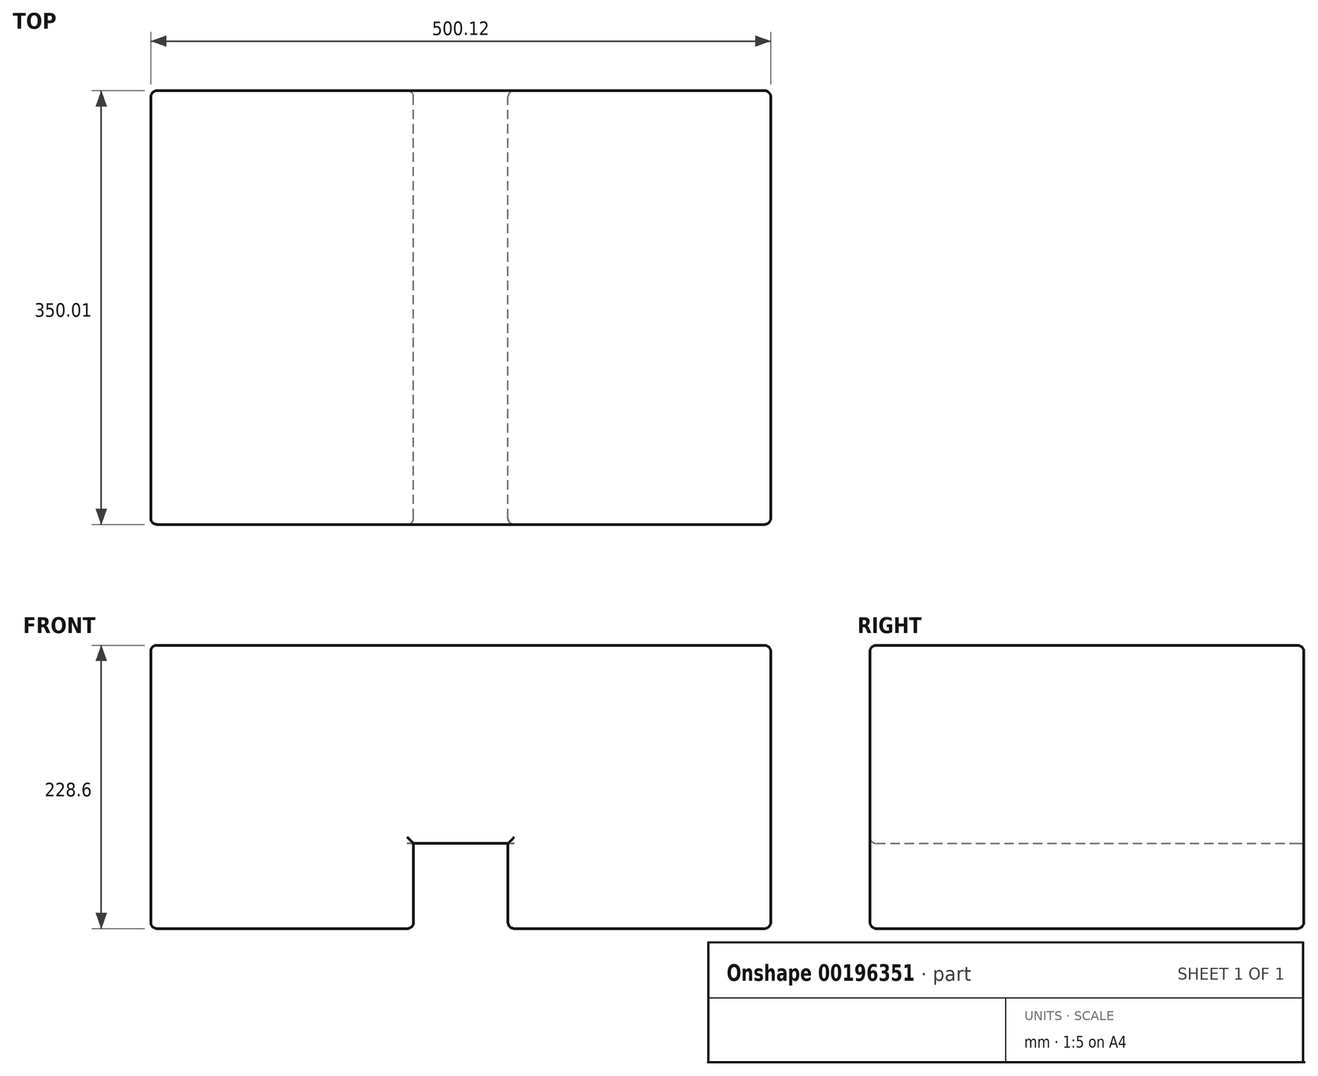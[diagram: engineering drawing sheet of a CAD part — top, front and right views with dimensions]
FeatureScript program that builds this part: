
annotation { "Feature Type Name" : "Feature", "Feature Type Description" : "" }
export const myFeature = defineFeature(function(context is Context, id is Id, definition is map)
    precondition{}
    {
        {
            var Q0;
            Q0=qCreatedBy(makeId("Front.planeOp"),FACE);
            var sketch = newSketch(context, id + "F0", { "sketchPlane" : qUnion([Q0])});
            skLineSegment(sketch, "E0.bottom", {"start": v(250.06, -114.3) * mm, "end": v(-250.06, -114.3) * mm});
            skLineSegment(sketch, "E0.top", {"start": v(250.06, 114.3) * mm, "end": v(-250.06, 114.3) * mm});
            skLineSegment(sketch, "E0.left", {"start": v(250.06, -114.3) * mm, "end": v(250.06, 114.3) * mm});
            skLineSegment(sketch, "E0.right", {"start": v(-250.06, -114.3) * mm, "end": v(-250.06, 114.3) * mm});
            skPoint(sketch, "E0.middle", {"position": v(0, 0) * mm});
            skSolve(sketch);
        }
        {
            var Q0;
            Q0 = qSketchRegion(id + "F0", true);
            extrude(context, id + "F1", {"entities" : qUnion([Q0]), "oppositeDirection" : true, "depth" : 350 * mm});
        }
        {
            var Q0;
            Q0=makeQuery(id+"F1.opExtrude","CAP_FACE",FACE,{"disambiguationData":[OSD([sQuery(id+"F0.wireOp",EDGE,"E0.bottom"),sQuery(id+"F0.wireOp",EDGE,"E0.top"),sQuery(id+"F0.wireOp",EDGE,"E0.left"),sQuery(id+"F0.wireOp",EDGE,"E0.right")])],"isStart":true});
            var Q1;
            Q1=makeQuery(id+"F1.opExtrude","SWEPT_FACE",FACE,{"disambiguationData":[OSD([sQuery(id+"F0.wireOp",EDGE,"E0.right")])]});
            var Q2;
            Q2=makeQuery(id+"F1.opExtrude","SWEPT_FACE",FACE,{"disambiguationData":[OSD([sQuery(id+"F0.wireOp",EDGE,"E0.top")])]});
            var Q3;
            Q3=makeQuery(id+"F1.opExtrude","SWEPT_FACE",FACE,{"disambiguationData":[OSD([sQuery(id+"F0.wireOp",EDGE,"E0.bottom")])]});
            var Q4;
            Q4=makeQuery(id+"F1.opExtrude","SWEPT_FACE",FACE,{"disambiguationData":[OSD([sQuery(id+"F0.wireOp",EDGE,"E0.left")])]});
            fillet(context, id + "F2", {"entities" : qUnion([Q0, Q1, Q2, Q3, Q4]), "radius" : 5.08 * mm, "tangentPropagation" : true, "allowEdgeOverflow" : false});
        }
        {
            var Q0;
            Q0=makeQuery(id+"F1.opExtrude","CAP_FACE",FACE,{"disambiguationData":[OSD([sQuery(id+"F0.wireOp",EDGE,"E0.bottom"),sQuery(id+"F0.wireOp",EDGE,"E0.top"),sQuery(id+"F0.wireOp",EDGE,"E0.left"),sQuery(id+"F0.wireOp",EDGE,"E0.right")])],"isStart":false});
            var sketch = newSketch(context, id + "F3", { "sketchPlane" : qUnion([Q0])});
            skLineSegment(sketch, "E1", {"start": v(0, 0) * mm, "end": v(0, -45.63) * mm});
            skLineSegment(sketch, "E2", {"start": v(0, -121.83) * mm, "end": v(0, -109.22) * mm});
            skLineSegment(sketch, "E3", {"start": v(38.1, -94.1) * mm, "end": v(39.87, -94.1) * mm});
            skLineSegment(sketch, "E4.bottom", {"start": v(38.1, -45.63) * mm, "end": v(-38.1, -45.63) * mm});
            skLineSegment(sketch, "E4.top", {"start": v(38.1, -121.83) * mm, "end": v(-38.1, -121.83) * mm});
            skLineSegment(sketch, "E4.left", {"start": v(38.1, -45.63) * mm, "end": v(38.1, -121.83) * mm});
            skLineSegment(sketch, "E4.right", {"start": v(-38.1, -45.63) * mm, "end": v(-38.1, -121.83) * mm});
            skPoint(sketch, "E4.middle", {"position": v(0, -83.73) * mm});
            skLineSegment(sketch, "E5.trimOffspring", {"start": v(0, -109.22) * mm, "end": v(0, -121.83) * mm});
            skSolve(sketch);
        }
        {
            var Q0;
            Q0 = qSketchRegion(id + "F3", true);
            extrude(context, id + "F4", {"entities" : qUnion([Q0]), "operationType" : NewBodyOperationType.REMOVE, "endBound" : BoundingType.THROUGH_ALL, "oppositeDirection" : true, "depth" : 101.6 * mm});
        }
        {
            var Q0;
            Q0=makeQuery(id+"F4.boolean.opBoolean","INTERSECT",EDGE,{"derivedFrom":[makeQuery(id+"F1.opExtrude","CAP_FACE",FACE,{"disambiguationData":[OSD([sQuery(id+"F0.wireOp",EDGE,"E0.bottom"),sQuery(id+"F0.wireOp",EDGE,"E0.top"),sQuery(id+"F0.wireOp",EDGE,"E0.left"),sQuery(id+"F0.wireOp",EDGE,"E0.right")])],"isStart":true}),makeQuery(id+"F4.opExtrude","SWEPT_FACE",FACE,{"disambiguationData":[OSD([sQuery(id+"F3.wireOp",EDGE,"E4.bottom")])]})]});
            var Q1;
            Q1=makeQuery(id+"F4.boolean.opBoolean","INTERSECT",EDGE,{"derivedFrom":[makeQuery(id+"F1.opExtrude","CAP_FACE",FACE,{"disambiguationData":[OSD([sQuery(id+"F0.wireOp",EDGE,"E0.bottom"),sQuery(id+"F0.wireOp",EDGE,"E0.top"),sQuery(id+"F0.wireOp",EDGE,"E0.left"),sQuery(id+"F0.wireOp",EDGE,"E0.right")])],"isStart":true}),makeQuery(id+"F4.opExtrude","SWEPT_FACE",FACE,{"disambiguationData":[OSD([sQuery(id+"F3.wireOp",EDGE,"E4.left")])]})]});
            var Q2;
            Q2=makeQuery(id+"F4.boolean.opBoolean","INTERSECT",EDGE,{"derivedFrom":[makeQuery(id+"F1.opExtrude","CAP_FACE",FACE,{"disambiguationData":[OSD([sQuery(id+"F0.wireOp",EDGE,"E0.bottom"),sQuery(id+"F0.wireOp",EDGE,"E0.top"),sQuery(id+"F0.wireOp",EDGE,"E0.left"),sQuery(id+"F0.wireOp",EDGE,"E0.right")])],"isStart":true}),makeQuery(id+"F4.opExtrude","SWEPT_FACE",FACE,{"disambiguationData":[OSD([sQuery(id+"F3.wireOp",EDGE,"E4.top")])]})]});
            var Q3;
            Q3=makeQuery(id+"F4.boolean.opBoolean","INTERSECT",EDGE,{"derivedFrom":[makeQuery(id+"F1.opExtrude","CAP_FACE",FACE,{"disambiguationData":[OSD([sQuery(id+"F0.wireOp",EDGE,"E0.bottom"),sQuery(id+"F0.wireOp",EDGE,"E0.top"),sQuery(id+"F0.wireOp",EDGE,"E0.left"),sQuery(id+"F0.wireOp",EDGE,"E0.right")])],"isStart":true}),makeQuery(id+"F4.opExtrude","SWEPT_FACE",FACE,{"disambiguationData":[OSD([sQuery(id+"F3.wireOp",EDGE,"E4.right")])]})]});
            var Q4;
            Q4=makeQuery(id+"F4.boolean.opBoolean","COPY",EDGE,{"derivedFrom":makeQuery(id+"F4.opExtrude","CAP_EDGE",EDGE,{"disambiguationData":[OSD([sQuery(id+"F3.wireOp",EDGE,"E4.left")])],"isStart":true})});
            var Q5;
            Q5=makeQuery(id+"F4.boolean.opBoolean","COPY",EDGE,{"derivedFrom":makeQuery(id+"F4.opExtrude","CAP_EDGE",EDGE,{"disambiguationData":[OSD([sQuery(id+"F3.wireOp",EDGE,"E4.bottom")])],"isStart":true})});
            var Q6;
            Q6=makeQuery(id+"F4.boolean.opBoolean","COPY",EDGE,{"derivedFrom":makeQuery(id+"F4.opExtrude","CAP_EDGE",EDGE,{"disambiguationData":[OSD([sQuery(id+"F3.wireOp",EDGE,"E4.right")])],"isStart":true})});
            var Q7;
            Q7=makeQuery(id+"F4.boolean.opBoolean","COPY",EDGE,{"derivedFrom":makeQuery(id+"F4.opExtrude","CAP_EDGE",EDGE,{"disambiguationData":[OSD([sQuery(id+"F3.wireOp",EDGE,"E4.top")])],"isStart":true})});
            fillet(context, id + "F5", {"entities" : qUnion([Q0, Q1, Q2, Q3, Q4, Q5, Q6, Q7]), "radius" : 5.08 * mm, "tangentPropagation" : true, "allowEdgeOverflow" : false});
        }
    });
